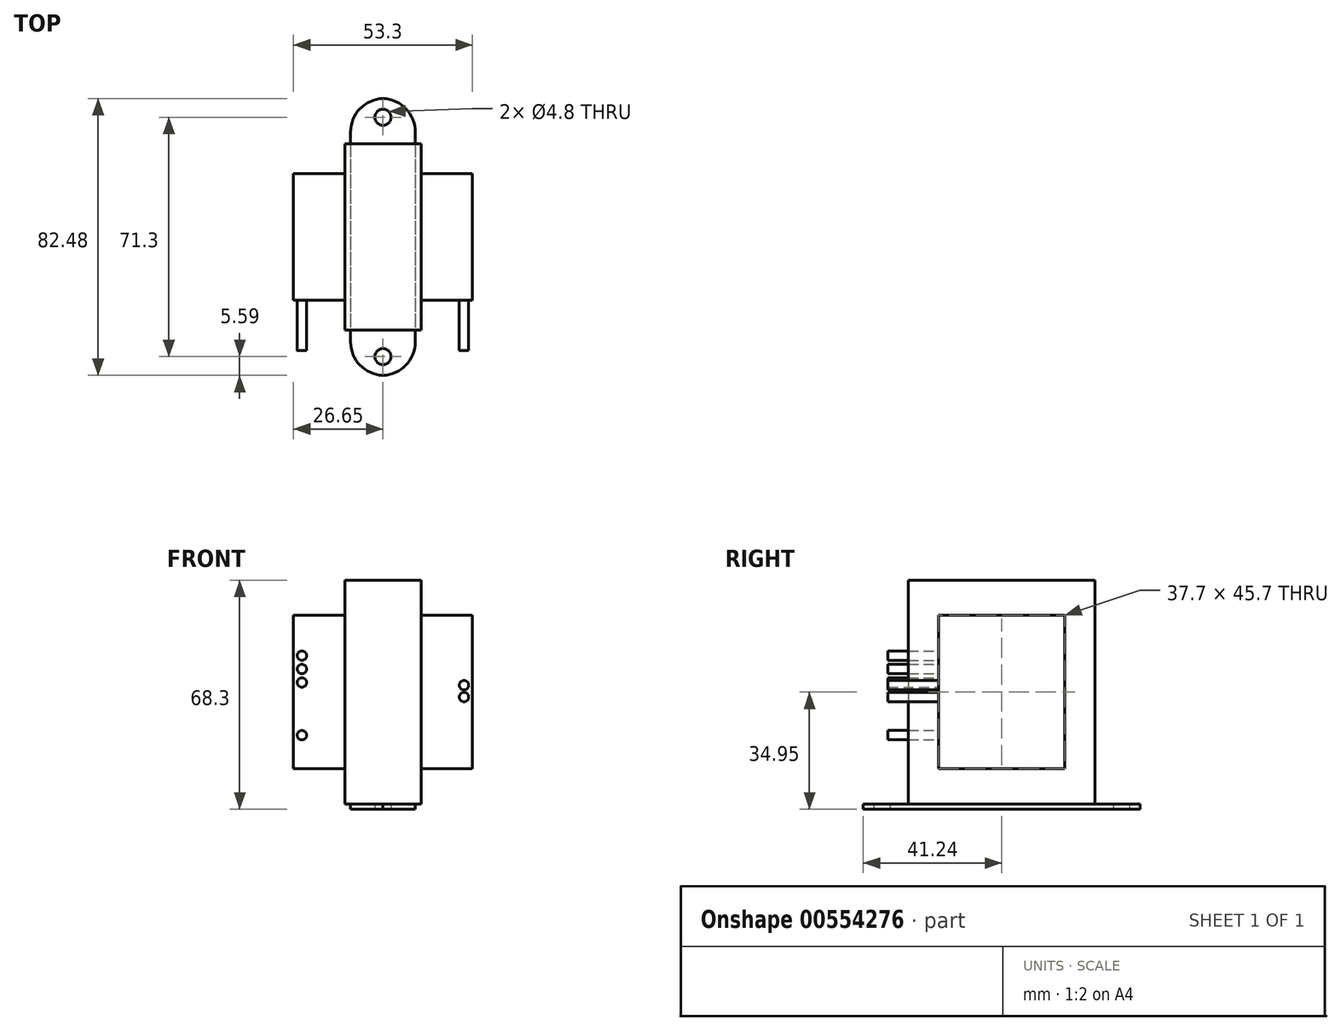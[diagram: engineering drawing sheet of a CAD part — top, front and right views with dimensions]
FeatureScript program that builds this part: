
annotation { "Feature Type Name" : "Feature", "Feature Type Description" : "" }
export const myFeature = defineFeature(function(context is Context, id is Id, definition is map)
    precondition{}
    {
        {
            var Q0;
            Q0=qCreatedBy(makeId("Top.planeOp"),FACE);
            var sketch = newSketch(context, id + "F0", { "sketchPlane" : qUnion([Q0])});
            skLineSegment(sketch, "E0.bottom", {"start": v(9.65, 41.25) * mm, "end": v(-9.65, 41.25) * mm});
            skLineSegment(sketch, "E0.top", {"start": v(9.65, -41.25) * mm, "end": v(-9.65, -41.25) * mm});
            skLineSegment(sketch, "E0.left", {"start": v(9.65, 41.25) * mm, "end": v(9.65, -41.25) * mm});
            skLineSegment(sketch, "E0.right", {"start": v(-9.65, 41.25) * mm, "end": v(-9.65, -41.25) * mm});
            skPoint(sketch, "E0.middle", {"position": v(0, 0) * mm});
            skSolve(sketch);
        }
        {
            var Q0;
            Q0=makeQuery(id+"F0.imprint","IMPRINT",FACE,{"disambiguationData":[TD([[makeQuery(id+"F0.imprint","IMPRINT",EDGE,{"derivedFrom":sQuery(id+"F0.wireOp",EDGE,"E0.bottom")}),1.0]])]});
            extrude(context, id + "F1", {"entities" : qUnion([Q0]), "depth" : 1.6 * mm, "offsetDistance" : 25 * mm});
        }
        {
            var Q0;
            Q0=makeQuery(id+"F1.opExtrude","CAP_FACE",FACE,{"disambiguationData":[OSD([sQuery(id+"F0.wireOp",EDGE,"E0.bottom"),sQuery(id+"F0.wireOp",EDGE,"E0.top"),sQuery(id+"F0.wireOp",EDGE,"E0.left"),sQuery(id+"F0.wireOp",EDGE,"E0.right")])],"isStart":false});
            var sketch = newSketch(context, id + "F2", { "sketchPlane" : qUnion([Q0])});
            skLineSegment(sketch, "E1.bottom", {"start": v(11.4, -27.8) * mm, "end": v(-11.4, -27.8) * mm});
            skLineSegment(sketch, "E1.top", {"start": v(11.4, 27.8) * mm, "end": v(-11.4, 27.8) * mm});
            skLineSegment(sketch, "E1.left", {"start": v(11.4, -27.8) * mm, "end": v(11.4, 27.8) * mm});
            skLineSegment(sketch, "E1.right", {"start": v(-11.4, -27.8) * mm, "end": v(-11.4, 27.8) * mm});
            skPoint(sketch, "E1.middle", {"position": v(0, 0) * mm});
            skSolve(sketch);
        }
        {
            var Q0;
            Q0 = qSketchRegion(id + "F2", true);
            extrude(context, id + "F3", {"entities" : qUnion([Q0]), "operationType" : NewBodyOperationType.ADD, "depth" : 66.7 * mm, "offsetDistance" : 25 * mm});
        }
        {
            var Q0;
            Q0=makeQuery(id+"F3.opExtrude","SWEPT_FACE",FACE,{"disambiguationData":[OSD([sQuery(id+"F2.wireOp",EDGE,"E1.right")])]});
            var sketch = newSketch(context, id + "F4", { "sketchPlane" : qUnion([Q0])});
            skLineSegment(sketch, "E2.bottom", {"start": v(18.85, 12.1) * mm, "end": v(-18.85, 12.1) * mm});
            skLineSegment(sketch, "E2.top", {"start": v(18.85, 57.8) * mm, "end": v(-18.85, 57.8) * mm});
            skLineSegment(sketch, "E2.left", {"start": v(18.85, 12.1) * mm, "end": v(18.85, 57.8) * mm});
            skLineSegment(sketch, "E2.right", {"start": v(-18.85, 12.1) * mm, "end": v(-18.85, 57.8) * mm});
            skPoint(sketch, "E2.middle", {"position": v(0, 34.95) * mm});
            skPoint(sketch, "E2.middle.positionSnap0", {"position": v(0, 1.6) * mm});
            skPoint(sketch, "E2.centerSnap0", {"position": v(0, 1.6) * mm});
            skSolve(sketch);
        }
        {
            var Q0;
            Q0 = qSketchRegion(id + "F4", true);
            extrude(context, id + "F5", {"entities" : qUnion([Q0]), "operationType" : NewBodyOperationType.ADD, "depth" : 15.25 * mm, "offsetDistance" : 25 * mm});
        }
        {
            var Q0;
            Q0=makeQuery(id+"F3.opExtrude","SWEPT_FACE",FACE,{"disambiguationData":[OSD([sQuery(id+"F2.wireOp",EDGE,"E1.left")])]});
            var sketch = newSketch(context, id + "F6", { "sketchPlane" : qUnion([Q0])});
            skLineSegment(sketch, "E3.bottom", {"start": v(18.85, 12.1) * mm, "end": v(-18.85, 12.1) * mm});
            skLineSegment(sketch, "E3.top", {"start": v(18.85, 57.8) * mm, "end": v(-18.85, 57.8) * mm});
            skLineSegment(sketch, "E3.left", {"start": v(18.85, 12.1) * mm, "end": v(18.85, 57.8) * mm});
            skLineSegment(sketch, "E3.right", {"start": v(-18.85, 12.1) * mm, "end": v(-18.85, 57.8) * mm});
            skPoint(sketch, "E3.middle", {"position": v(0, 34.95) * mm});
            skPoint(sketch, "E3.middle.positionSnap0", {"position": v(0, 1.6) * mm});
            skPoint(sketch, "E3.centerSnap0", {"position": v(0, 1.6) * mm});
            skSolve(sketch);
        }
        {
            var Q0;
            Q0 = qSketchRegion(id + "F6", true);
            extrude(context, id + "F7", {"entities" : qUnion([Q0]), "operationType" : NewBodyOperationType.ADD, "depth" : 15.25 * mm, "offsetDistance" : 25 * mm});
        }
        {
            var Q0;
            Q0=makeQuery(id+"F1.opExtrude","CAP_FACE",FACE,{"disambiguationData":[OSD([sQuery(id+"F0.wireOp",EDGE,"E0.bottom"),sQuery(id+"F0.wireOp",EDGE,"E0.top"),sQuery(id+"F0.wireOp",EDGE,"E0.left"),sQuery(id+"F0.wireOp",EDGE,"E0.right")])],"isStart":true});
            var sketch = newSketch(context, id + "F8", { "sketchPlane" : qUnion([Q0])});
            skCircle(sketch, "E4", {"center": v(0, 35.65) * mm, "radius": 2.4 * mm});
            skCircle(sketch, "E5", {"center": v(0, -35.65) * mm, "radius": 2.4 * mm});
            skSolve(sketch);
        }
        {
            var Q0;
            Q0 = qSketchRegion(id + "F8", true);
            extrude(context, id + "F9", {"entities" : qUnion([Q0]), "operationType" : NewBodyOperationType.REMOVE, "endBound" : BoundingType.THROUGH_ALL, "oppositeDirection" : true, "depth" : 25 * mm, "offsetDistance" : 25 * mm});
        }
        {
            var Q0;
            Q0=makeQuery(id+"F1.opExtrude","SWEPT_EDGE",EDGE,{"disambiguationData":[OSD([sQuery(id+"F0.wireOp",EDGE,"E0.bottom"),sQuery(id+"F0.wireOp",EDGE,"E0.right")])]});
            var Q1;
            Q1=makeQuery(id+"F1.opExtrude","SWEPT_EDGE",EDGE,{"disambiguationData":[OSD([sQuery(id+"F0.wireOp",EDGE,"E0.bottom"),sQuery(id+"F0.wireOp",EDGE,"E0.left")])]});
            var Q2;
            Q2=makeQuery(id+"F1.opExtrude","SWEPT_EDGE",EDGE,{"disambiguationData":[OSD([sQuery(id+"F0.wireOp",EDGE,"E0.top"),sQuery(id+"F0.wireOp",EDGE,"E0.left")])]});
            var Q3;
            Q3=makeQuery(id+"F1.opExtrude","SWEPT_EDGE",EDGE,{"disambiguationData":[OSD([sQuery(id+"F0.wireOp",EDGE,"E0.top"),sQuery(id+"F0.wireOp",EDGE,"E0.right")])]});
            fillet(context, id + "F10", {"entities" : qUnion([Q0, Q1, Q2, Q3]), "radius" : 10 * mm, "tangentPropagation" : true, "allowEdgeOverflow" : false});
        }
        {
            var Q0;
            Q0=makeQuery(id+"F5.opExtrude","SWEPT_FACE",FACE,{"disambiguationData":[OSD([sQuery(id+"F4.wireOp",EDGE,"E2.left")])]});
            var sketch = newSketch(context, id + "F11", { "sketchPlane" : qUnion([Q0])});
            skCircle(sketch, "E6", {"center": v(-24.15, 41.8) * mm, "radius": 1.4 * mm});
            skCircle(sketch, "E7", {"center": v(-24.15, 45.8) * mm, "radius": 1.4 * mm});
            skCircle(sketch, "E8", {"center": v(-24.15, 37.8) * mm, "radius": 1.4 * mm});
            skCircle(sketch, "E9", {"center": v(-24.15, 22.1) * mm, "radius": 1.4 * mm});
            skSolve(sketch);
        }
        {
            var Q0;
            Q0 = qSketchRegion(id + "F11", true);
            extrude(context, id + "F12", {"entities" : qUnion([Q0]), "operationType" : NewBodyOperationType.ADD, "depth" : 15 * mm, "offsetDistance" : 25 * mm});
        }
        {
            var Q0;
            Q0=makeQuery(id+"F7.opExtrude","SWEPT_FACE",FACE,{"disambiguationData":[OSD([sQuery(id+"F6.wireOp",EDGE,"E3.right")])]});
            var sketch = newSketch(context, id + "F13", { "sketchPlane" : qUnion([Q0])});
            skCircle(sketch, "E10", {"center": v(24.15, 36.97) * mm, "radius": 1.4 * mm});
            skCircle(sketch, "E11", {"center": v(24.15, 33.47) * mm, "radius": 1.4 * mm});
            skSolve(sketch);
        }
        {
            var Q0;
            Q0 = qSketchRegion(id + "F13", true);
            extrude(context, id + "F14", {"entities" : qUnion([Q0]), "operationType" : NewBodyOperationType.ADD, "depth" : 15 * mm, "offsetDistance" : 25 * mm});
        }
    });
